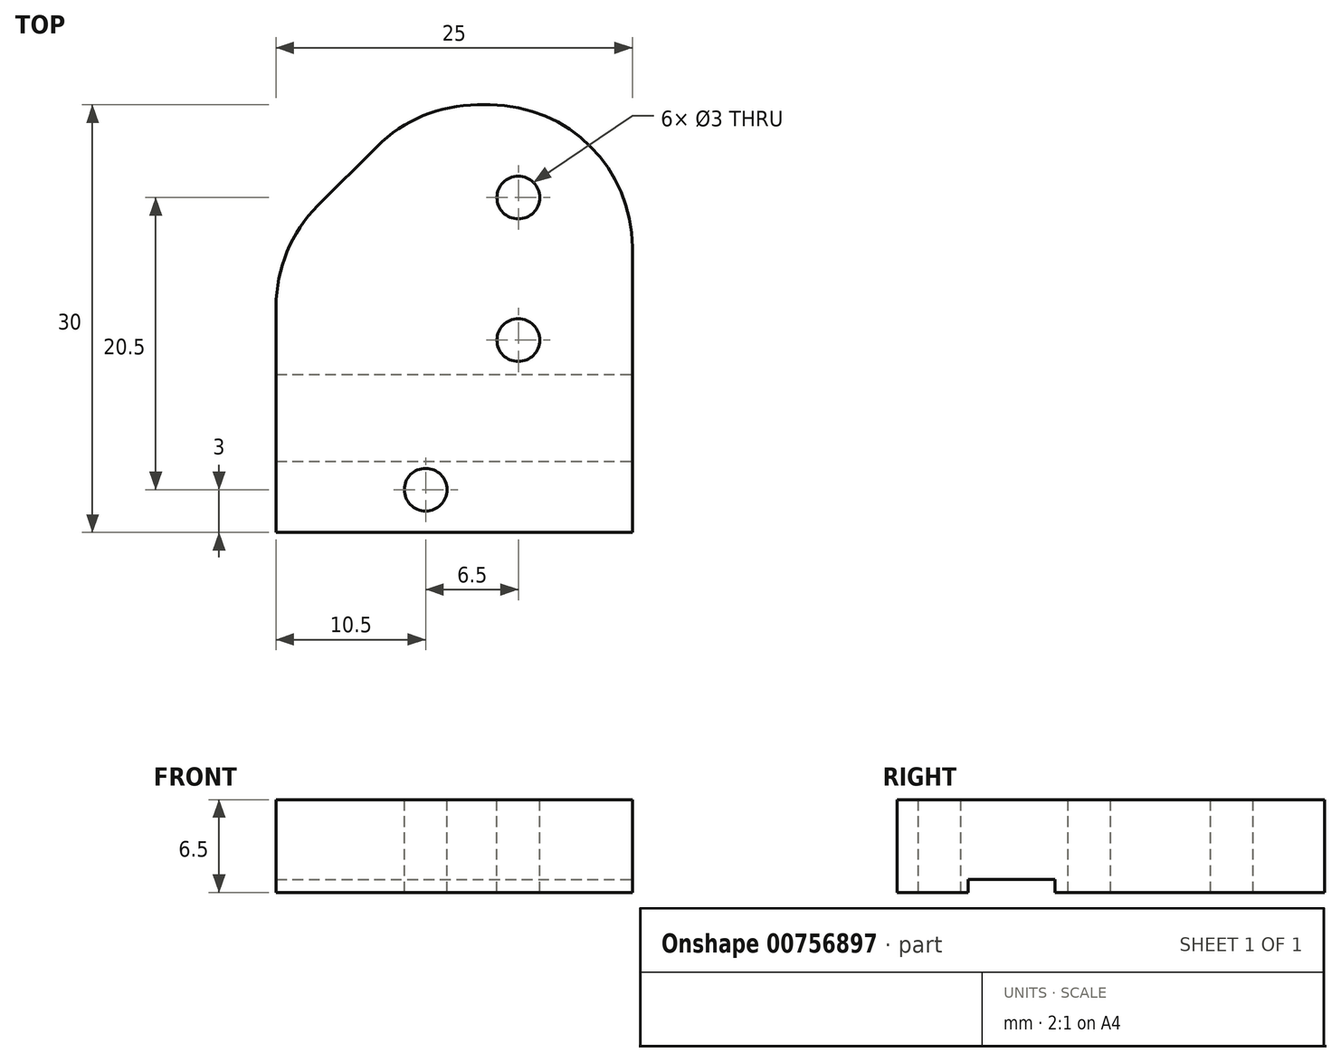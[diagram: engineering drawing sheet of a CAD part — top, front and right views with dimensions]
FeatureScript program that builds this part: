
annotation { "Feature Type Name" : "Feature", "Feature Type Description" : "" }
export const myFeature = defineFeature(function(context is Context, id is Id, definition is map)
    precondition{}
    {
        {
            var Q0;
            Q0=qCreatedBy(makeId("Top.planeOp"),FACE);
            var sketch = newSketch(context, id + "F0", { "sketchPlane" : qUnion([Q0])});
            skLineSegment(sketch, "E0.bottom", {"start": v(12.5, -15) * mm, "end": v(-12.5, -15) * mm});
            skLineSegment(sketch, "E0.top", {"start": v(12.5, 15) * mm, "end": v(-12.5, 15) * mm});
            skLineSegment(sketch, "E0.left", {"start": v(12.5, -15) * mm, "end": v(12.5, 15) * mm});
            skLineSegment(sketch, "E0.right", {"start": v(-12.5, -15) * mm, "end": v(-12.5, 15) * mm});
            skPoint(sketch, "E0.middle", {"position": v(0, 0) * mm});
            skSolve(sketch);
        }
        {
            var Q0;
            Q0=makeQuery(id+"F0.imprint","IMPRINT",FACE,{"disambiguationData":[TD([[makeQuery(id+"F0.imprint","IMPRINT",EDGE,{"derivedFrom":sQuery(id+"F0.wireOp",EDGE,"E0.bottom")}),-1.0]])]});
            extrude(context, id + "F1", {"entities" : qUnion([Q0]), "depth" : 6.5 * mm, "offsetDistance" : 25 * mm});
        }
        {
            var Q0;
            Q0=makeQuery(id+"F1.opExtrude","CAP_FACE",FACE,{"disambiguationData":[OSD([sQuery(id+"F0.wireOp",EDGE,"E0.bottom"),sQuery(id+"F0.wireOp",EDGE,"E0.top"),sQuery(id+"F0.wireOp",EDGE,"E0.left"),sQuery(id+"F0.wireOp",EDGE,"E0.right")])],"isStart":false});
            var sketch = newSketch(context, id + "F2", { "sketchPlane" : qUnion([Q0])});
            skCircle(sketch, "E1", {"center": v(-2, -12) * mm, "radius": 1.5 * mm});
            skPoint(sketch, "E1.centerSnap0", {"position": v(0, -15) * mm});
            skCircle(sketch, "E2", {"center": v(4.5, -1.5) * mm, "radius": 1.5 * mm});
            skCircle(sketch, "E3", {"center": v(4.5, 8.5) * mm, "radius": 1.5 * mm});
            skSolve(sketch);
        }
        {
            var Q0;
            Q0=qSketchRegion(id+"F2",true);
            extrude(context, id + "F3", {"entities" : qUnion([Q0]), "operationType" : NewBodyOperationType.REMOVE, "endBound" : BoundingType.THROUGH_ALL, "oppositeDirection" : true, "depth" : 25 * mm, "offsetDistance" : 25 * mm});
        }
        {
            var Q0;
            Q0=makeQuery(id+"F1.opExtrude","CAP_FACE",FACE,{"disambiguationData":[OSD([sQuery(id+"F0.wireOp",EDGE,"E0.bottom"),sQuery(id+"F0.wireOp",EDGE,"E0.top"),sQuery(id+"F0.wireOp",EDGE,"E0.left"),sQuery(id+"F0.wireOp",EDGE,"E0.right")])],"isStart":true});
            var sketch = newSketch(context, id + "F4", { "sketchPlane" : qUnion([Q0])});
            skLineSegment(sketch, "E4.bottom", {"start": v(-12.5, 10) * mm, "end": v(12.5, 10) * mm});
            skLineSegment(sketch, "E4.top", {"start": v(-12.5, 3.9) * mm, "end": v(12.5, 3.9) * mm});
            skLineSegment(sketch, "E4.left", {"start": v(-12.5, 10) * mm, "end": v(-12.5, 3.9) * mm});
            skLineSegment(sketch, "E4.right", {"start": v(12.5, 10) * mm, "end": v(12.5, 3.9) * mm});
            skPoint(sketch, "E4.middle", {"position": v(0, 6.95) * mm});
            skSolve(sketch);
        }
        {
            var Q0;
            Q0 = qSketchRegion(id + "F4", true);
            extrude(context, id + "F5", {"entities" : qUnion([Q0]), "operationType" : NewBodyOperationType.REMOVE, "oppositeDirection" : true, "depth" : 0.9 * mm, "offsetDistance" : 25 * mm});
        }
        {
            var Q0;
            Q0=makeQuery(id+"F1.opExtrude","SWEPT_EDGE",EDGE,{"disambiguationData":[OSD([sQuery(id+"F0.wireOp",EDGE,"E0.top"),sQuery(id+"F0.wireOp",EDGE,"E0.right")])]});
            chamfer(context, id + "F6", {"entities" : qUnion([Q0]), "width" : 10 * mm, "tangentPropagation" : true});
        }
        {
            var Q0;
            {var subQ0=sQuery(id+"F0.wireOp",EDGE,"E0.right");Q0=makeQuery(id+"F6.opChamfer","BLEND_EDGE",EDGE,{"blendedFrom":[makeQuery(id+"F1.opExtrude","SWEPT_EDGE",EDGE,{"disambiguationData":[OSD([sQuery(id+"F0.wireOp",EDGE,"E0.top"),subQ0])]}),makeQuery(id+"F1.opExtrude","SWEPT_FACE",FACE,{"disambiguationData":[OSD([subQ0])]})],"blendedInto":[makeQuery(id+"F1.opExtrude","SWEPT_FACE",FACE,{"disambiguationData":[OSD([subQ0])]})]});}
            var Q1;
            {var subQ0=sQuery(id+"F0.wireOp",EDGE,"E0.top");Q1=makeQuery(id+"F6.opChamfer","BLEND_EDGE",EDGE,{"blendedFrom":[makeQuery(id+"F1.opExtrude","SWEPT_EDGE",EDGE,{"disambiguationData":[OSD([subQ0,sQuery(id+"F0.wireOp",EDGE,"E0.right")])]}),makeQuery(id+"F1.opExtrude","SWEPT_FACE",FACE,{"disambiguationData":[OSD([subQ0])]})],"blendedInto":[makeQuery(id+"F1.opExtrude","SWEPT_FACE",FACE,{"disambiguationData":[OSD([subQ0])]})]});}
            var Q2;
            Q2=makeQuery(id+"F1.opExtrude","SWEPT_EDGE",EDGE,{"disambiguationData":[OSD([sQuery(id+"F0.wireOp",EDGE,"E0.top"),sQuery(id+"F0.wireOp",EDGE,"E0.left")])]});
            fillet(context, id + "F7", {"entities" : qUnion([Q0, Q1, Q2]), "radius" : 10 * mm, "tangentPropagation" : true, "allowEdgeOverflow" : false});
        }
    });
